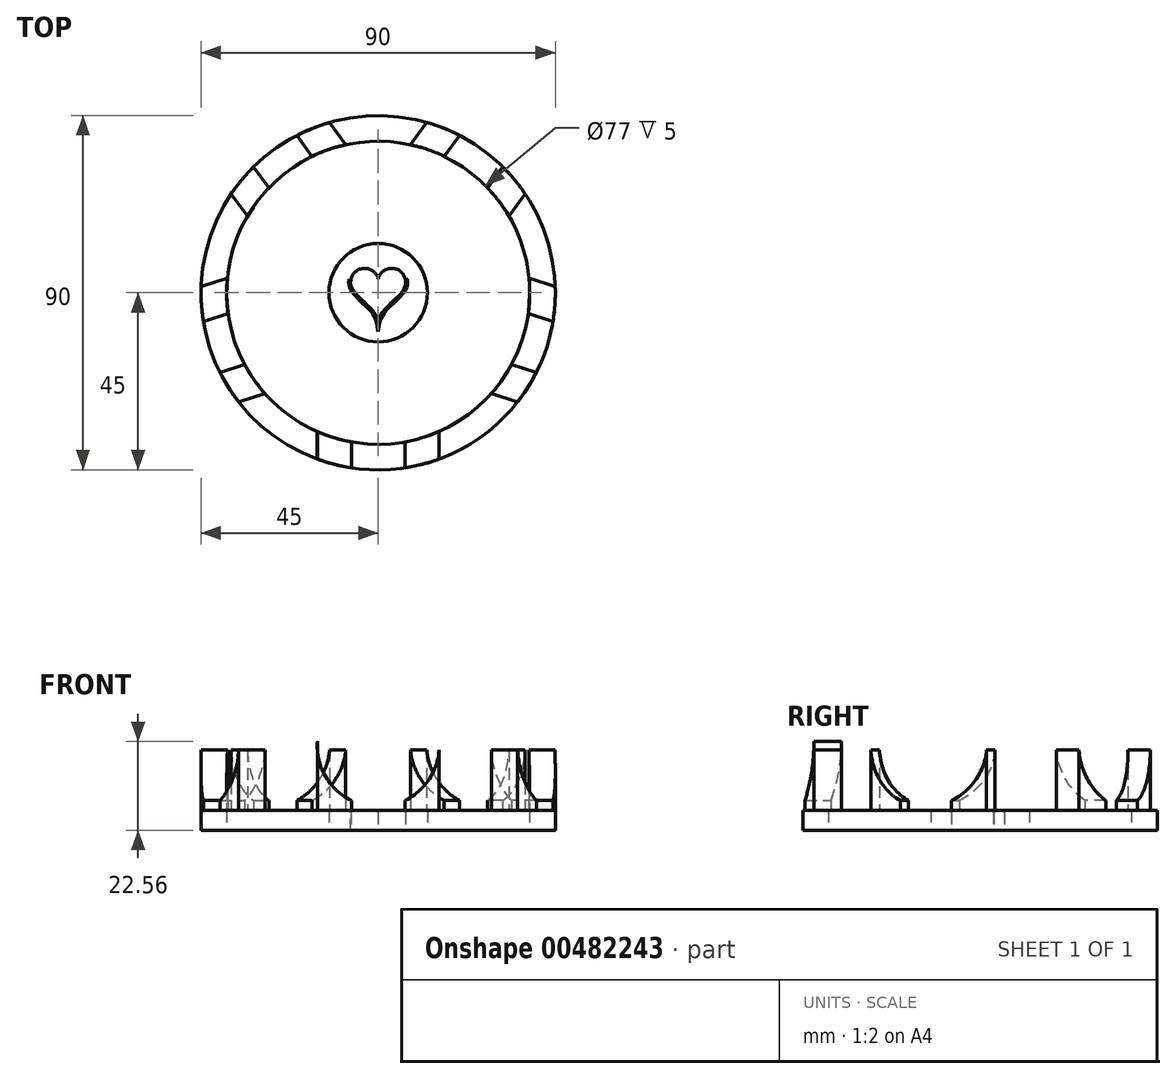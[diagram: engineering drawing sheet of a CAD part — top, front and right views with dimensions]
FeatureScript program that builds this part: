
annotation { "Feature Type Name" : "Feature", "Feature Type Description" : "" }
export const myFeature = defineFeature(function(context is Context, id is Id, definition is map)
    precondition{}
    {
        {
            var Q0;
            Q0=qCreatedBy(makeId("Top.planeOp"),FACE);
            var sketch = newSketch(context, id + "F0", { "sketchPlane" : qUnion([Q0])});
            skCircle(sketch, "E0", {"center": v(0, 0) * mm, "radius": 45 * mm});
            skCircle(sketch, "E1", {"center": v(0, 0) * mm, "radius": 12.5 * mm});
            skCircle(sketch, "E2", {"center": v(0, 0) * mm, "radius": 38.5 * mm});
            skFitSpline(sketch, "E3", {"points": [v(-23.43, -30.55) * mm, v(-6.82, -10.48) * mm], "startDerivative": vector(57.5, -25.64) * mm, "endDerivative": vector(34.47, -7.7) * mm});
            skFitSpline(sketch, "E4", {"points": [v(-11.77, -4.23) * mm, v(-32.93, -19.95) * mm], "startDerivative": vector(-33.1, 12.7) * mm, "endDerivative": vector(-63.94, 45.6) * mm});
            skArc(sketch, "E5", {"start": v(0, 3.51) * mm, "mid": v(-3.53, 6.2) * mm, "end": v(-6.92, 3.34) * mm});
            skArc(sketch, "E6.MirrorCS", {"start": v(0, 3.51) * mm, "mid": v(3.53, 6.2) * mm, "end": v(6.92, 3.34) * mm});
            skFitSpline(sketch, "E7", {"points": [v(0, -7.29) * mm, v(-6.92, 3.34) * mm], "startDerivative": vector(-2.6, 13.19) * mm, "endDerivative": vector(2.72, 11.93) * mm});
            skFitSpline(sketch, "E8.MirrorCS", {"points": [v(0, -7.29) * mm, v(6.92, 3.34) * mm], "startDerivative": vector(2.6, 13.19) * mm, "endDerivative": vector(-2.72, 11.93) * mm});
            skCircle(sketch, "E9", {"center": v(0, 0) * mm, "radius": 56.48 * mm});
            skSolve(sketch);
        }
        {
            var Q0;
            {var subQ0=sQuery(id+"F0.wireOp",EDGE,"E3");Q0=makeQuery(id+"F0.imprint","IMPRINT",FACE,{"disambiguationData":[TD([[makeQuery(id+"F0.imprint","IMPRINT",EDGE,{"derivedFrom":subQ0}),1.0]])]});}
            extrude(context, id + "F1", {"entities" : qUnion([Q0]), "depth" : 5 * mm});
        }
        {
            var Q0;
            Q0=makeQuery(id+"F1.opExtrude","SWEPT_BODY",BODY,{"disambiguationData":[OSD([sQuery(id+"F0.wireOp",EDGE,"E1"),sQuery(id+"F0.wireOp",EDGE,"E2"),sQuery(id+"F0.wireOp",EDGE,"E3"),sQuery(id+"F0.wireOp",EDGE,"E4")])]});
            var Q1;
            Q1=sQuery(id+"F0.wireOp",EDGE,"E1");
            circularPattern(context, id + "F2", {"entities" : qUnion([Q0]), "axis" : qUnion([Q1]), "angle" : 360 * degree, "instanceCount" : 8, "equalSpace" : true});
        }
        {
            var Q0;
            Q0=makeQuery(id+"F0.imprint","IMPRINT",FACE,{"disambiguationData":[TD([[makeQuery(id+"F0.imprint","IMPRINT",EDGE,{"derivedFrom":sQuery(id+"F0.wireOp",EDGE,"E0")}),1.0]])]});
            extrude(context, id + "F3", {"entities" : qUnion([Q0]), "depth" : 5 * mm});
        }
        {
            var Q0;
            Q0=makeQuery(id+"F0.imprint","IMPRINT",FACE,{"disambiguationData":[TD([[makeQuery(id+"F0.imprint","IMPRINT",EDGE,{"derivedFrom":sQuery(id+"F0.wireOp",EDGE,"E5")}),-1.0]])]});
            extrude(context, id + "F4", {"entities" : qUnion([Q0]), "depth" : 5 * mm});
        }
        {
            var Q0;
            Q0=makeQuery(id+"F4.opExtrude","CAP_EDGE",EDGE,{"disambiguationData":[OSD([sQuery(id+"F0.wireOp",EDGE,"E6.MirrorCS")])],"isStart":false});
            var Q1;
            Q1=makeQuery(id+"F4.opExtrude","CAP_EDGE",EDGE,{"disambiguationData":[OSD([sQuery(id+"F0.wireOp",EDGE,"E5")])],"isStart":false});
            var Q2;
            Q2=makeQuery(id+"F4.opExtrude","CAP_EDGE",EDGE,{"disambiguationData":[OSD([sQuery(id+"F0.wireOp",EDGE,"E7")])],"isStart":false});
            var Q3;
            Q3=makeQuery(id+"F4.opExtrude","CAP_EDGE",EDGE,{"disambiguationData":[OSD([sQuery(id+"F0.wireOp",EDGE,"E8.MirrorCS")])],"isStart":false});
            fillet(context, id + "F5", {"entities" : qUnion([Q0, Q1, Q2, Q3]), "radius" : 0.5 * mm, "tangentPropagation" : true, "allowEdgeOverflow" : false});
        }
        {
            var Q0;
            Q0=qCreatedBy(makeId("Front.planeOp"),FACE);
            var sketch = newSketch(context, id + "F6", { "sketchPlane" : qUnion([Q0])});
            skCircle(sketch, "E10", {"center": v(0, 21.47) * mm, "radius": 15.48 * mm});
            skLineSegment(sketch, "E11", {"start": v(-15.45, 22.56) * mm, "end": v(-15.45, 0) * mm});
            skLineSegment(sketch, "E12", {"start": v(-15.45, 0) * mm, "end": v(0, 0) * mm});
            skLineSegment(sketch, "E13.MirrorCS", {"start": v(15.45, 22.56) * mm, "end": v(15.45, 0) * mm});
            skLineSegment(sketch, "E14.MirrorCS", {"start": v(15.45, 0) * mm, "end": v(0, 0) * mm});
            skCircle(sketch, "E15", {"center": v(0, 21.47) * mm, "radius": 6.8 * mm});
            skLineSegment(sketch, "E16", {"start": v(-6.8, 21.66) * mm, "end": v(-6.8, 7.56) * mm});
            skLineSegment(sketch, "E17.MirrorCS", {"start": v(6.8, 21.66) * mm, "end": v(6.8, 7.56) * mm});
            skLineSegment(sketch, "E18", {"start": v(-6.8, 7.56) * mm, "end": v(-6.8, 0) * mm});
            skLineSegment(sketch, "E19.MirrorCS", {"start": v(6.8, 7.56) * mm, "end": v(6.8, 0) * mm});
            skLineSegment(sketch, "E20", {"start": v(-15.45, 5) * mm, "end": v(15.45, 5) * mm});
            skSolve(sketch);
        }
        {
            var Q0;
            {var subQ3=sQuery(id+"F6.wireOp",EDGE,"E11");var subQ5=sQuery(id+"F6.wireOp",EDGE,"E20");var subQ6=makeQuery(id+"F6.imprint","INTERSECT",VERTEX,{"derivedFrom":[subQ3,subQ5]});Q0=makeQuery(id+"F6.imprint","IMPRINT",FACE,{"disambiguationData":[TD([[makeQuery(id+"F6.imprint","IMPRINT",EDGE,{"disambiguationData":[TD([[subQ6,1.0]])],"derivedFrom":subQ3}),1.0]])]});}
            var Q1;
            {var subQ3=sQuery(id+"F6.wireOp",EDGE,"E13.MirrorCS");var subQ5=sQuery(id+"F6.wireOp",EDGE,"E20");var subQ6=makeQuery(id+"F6.imprint","INTERSECT",VERTEX,{"derivedFrom":[subQ3,subQ5]});Q1=makeQuery(id+"F6.imprint","IMPRINT",FACE,{"disambiguationData":[TD([[makeQuery(id+"F6.imprint","IMPRINT",EDGE,{"disambiguationData":[TD([[subQ6,1.0]])],"derivedFrom":subQ3}),-1.0]])]});}
            var Q2;
            {var subQ0=sQuery(id+"F6.wireOp",EDGE,"E11");var subQ1=sQuery(id+"F6.wireOp",EDGE,"E10");var subQ2=makeQuery(id+"F6.imprint","INTERSECT",VERTEX,{"disambiguationData":[OD(0.0)],"derivedFrom":[subQ1,subQ0]});Q2=makeQuery(id+"F6.imprint","IMPRINT",FACE,{"disambiguationData":[TD([[makeQuery(id+"F6.imprint","IMPRINT",EDGE,{"disambiguationData":[TD([[subQ2,1.0]])],"derivedFrom":subQ1}),1.0]])]});}
            extrude(context, id + "F7", {"entities" : qUnion([Q0, Q1, Q2]), "depth" : 47.5 * mm, "hasSecondDirection" : true, "secondDirectionOppositeDirection" : false, "secondDirectionDepth" : 33.9 * mm});
        }
        {
            var Q0;
            Q0=makeQuery(id+"F0.imprint","IMPRINT",FACE,{"disambiguationData":[TD([[makeQuery(id+"F0.imprint","IMPRINT",EDGE,{"derivedFrom":sQuery(id+"F0.wireOp",EDGE,"E0")}),-1.0]])]});
            var Q1;
            {var subQ0=sQuery(id+"F0.wireOp",EDGE,"E3");Q1=makeQuery(id+"F0.imprint","IMPRINT",FACE,{"disambiguationData":[TD([[makeQuery(id+"F0.imprint","IMPRINT",EDGE,{"derivedFrom":subQ0}),-1.0]])]});}
            var Q2;
            {var subQ0=sQuery(id+"F0.wireOp",EDGE,"E3");Q2=makeQuery(id+"F0.imprint","IMPRINT",FACE,{"disambiguationData":[TD([[makeQuery(id+"F0.imprint","IMPRINT",EDGE,{"derivedFrom":subQ0}),1.0]])]});}
            extrude(context, id + "F8", {"entities" : qUnion([Q0, Q1, Q2]), "operationType" : NewBodyOperationType.REMOVE, "depth" : 41 * mm});
        }
        {
            var Q0;
            Q0=makeQuery(id+"F7.opExtrude","SWEPT_BODY",BODY,{"disambiguationData":[OSD([sQuery(id+"F6.wireOp",EDGE,"E10"),sQuery(id+"F6.wireOp",EDGE,"E11"),sQuery(id+"F6.wireOp",EDGE,"E13.MirrorCS"),sQuery(id+"F6.wireOp",EDGE,"E15"),sQuery(id+"F6.wireOp",EDGE,"E16"),sQuery(id+"F6.wireOp",EDGE,"E17.MirrorCS"),sQuery(id+"F6.wireOp",EDGE,"E18"),sQuery(id+"F6.wireOp",EDGE,"E19.MirrorCS"),sQuery(id+"F6.wireOp",EDGE,"E20")])]});
            var Q1;
            Q1=makeQuery(id+"F3.opExtrude","CAP_EDGE",EDGE,{"disambiguationData":[OSD([sQuery(id+"F0.wireOp",EDGE,"E2")])],"isStart":false});
            circularPattern(context, id + "F9", {"entities" : qUnion([Q0]), "axis" : qUnion([Q1]), "angle" : 360 * degree, "instanceCount" : 5, "equalSpace" : true});
        }
    });
